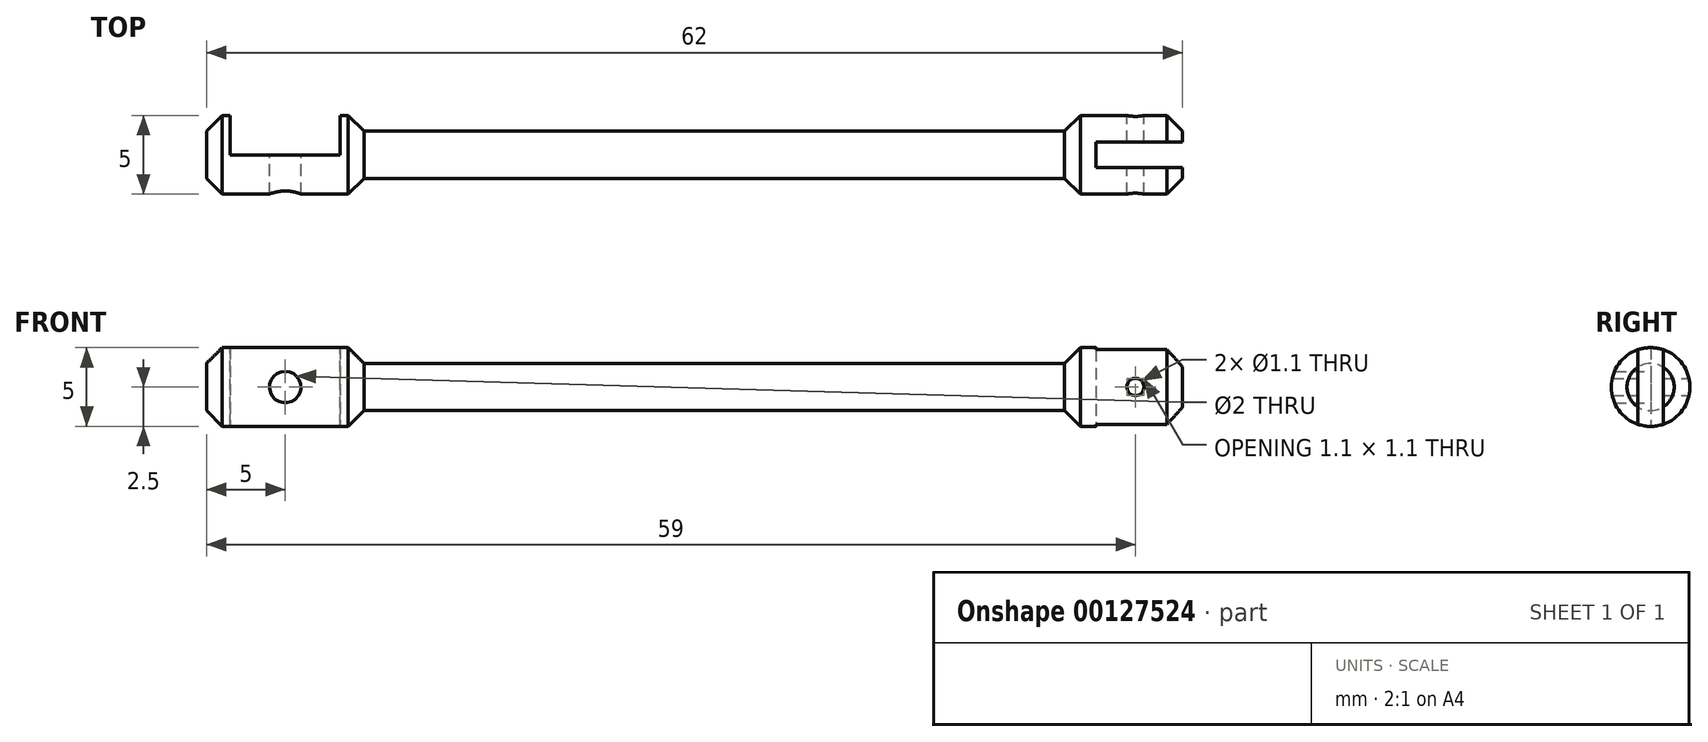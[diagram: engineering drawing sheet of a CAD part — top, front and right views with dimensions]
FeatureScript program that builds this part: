
annotation { "Feature Type Name" : "Feature", "Feature Type Description" : "" }
export const myFeature = defineFeature(function(context is Context, id is Id, definition is map)
    precondition{}
    {
        {
            var Q0;
            Q0=qCreatedBy(makeId("Front.planeOp"),FACE);
            var sketch = newSketch(context, id + "F0", { "sketchPlane" : qUnion([Q0])});
            skCircle(sketch, "E0", {"center": v(0, 0) * mm, "radius": 1 * mm});
            skCircle(sketch, "E1", {"center": v(54, 0) * mm, "radius": 0.55 * mm});
            skLineSegment(sketch, "E2", {"start": v(-5, 0) * mm, "end": v(57, 0) * mm});
            skLineSegment(sketch, "E3", {"start": v(57, 0) * mm, "end": v(57, 1.5) * mm});
            skLineSegment(sketch, "E4", {"start": v(56, 2.5) * mm, "end": v(50.5, 2.5) * mm});
            skLineSegment(sketch, "E5", {"start": v(49.5, 1.5) * mm, "end": v(5, 1.5) * mm});
            skLineSegment(sketch, "E6", {"start": v(4, 2.5) * mm, "end": v(-4, 2.5) * mm});
            skLineSegment(sketch, "E7", {"start": v(-5, 1.5) * mm, "end": v(-5, 0) * mm});
            skLineSegment(sketch, "E8", {"start": v(56, 2.5) * mm, "end": v(57, 1.5) * mm});
            skLineSegment(sketch, "E9", {"start": v(49.5, 1.5) * mm, "end": v(50.5, 2.5) * mm});
            skLineSegment(sketch, "E10", {"start": v(0, 0) * mm, "end": v(0, 0) * mm});
            skLineSegment(sketch, "E11", {"start": v(4, 2.5) * mm, "end": v(5, 1.5) * mm});
            skLineSegment(sketch, "E12", {"start": v(-4, 2.5) * mm, "end": v(-5, 1.5) * mm});
            skSolve(sketch);
        }
        {
            var Q0;
            {var subQ0=sQuery(id+"F0.wireOp",EDGE,"E3");Q0=makeQuery(id+"F0.imprint","IMPRINT",FACE,{"disambiguationData":[TD([[makeQuery(id+"F0.imprint","IMPRINT",EDGE,{"derivedFrom":subQ0}),1.0]])]});}
            var Q1;
            {var subQ0=sQuery(id+"F0.wireOp",EDGE,"E2");var subQ1=sQuery(id+"F0.wireOp",EDGE,"E0");var subQ2=makeQuery(id+"F0.imprint","INTERSECT",VERTEX,{"disambiguationData":[OD(0.0)],"derivedFrom":[subQ1,subQ0]});Q1=makeQuery(id+"F0.imprint","IMPRINT",FACE,{"disambiguationData":[TD([[makeQuery(id+"F0.imprint","IMPRINT",EDGE,{"disambiguationData":[TD([[subQ2,1.0]])],"derivedFrom":subQ1}),1.0]])]});}
            var Q2;
            {var subQ0=sQuery(id+"F0.wireOp",EDGE,"E2");var subQ1=sQuery(id+"F0.wireOp",EDGE,"E1");var subQ2=makeQuery(id+"F0.imprint","INTERSECT",VERTEX,{"disambiguationData":[OD(0.0)],"derivedFrom":[subQ1,subQ0]});Q2=makeQuery(id+"F0.imprint","IMPRINT",FACE,{"disambiguationData":[TD([[makeQuery(id+"F0.imprint","IMPRINT",EDGE,{"disambiguationData":[TD([[subQ2,1.0]])],"derivedFrom":subQ1}),1.0]])]});}
            var Q3;
            Q3=sQuery(id+"F0.wireOp",EDGE,"E2");
            revolve(context, id + "F1", {"entities" : qUnion([Q0, Q1, Q2]), "axis" : qUnion([Q3]), "revolveType" : RevolveType.FULL});
        }
        {
            var Q0;
            {var subQ0=sQuery(id+"F0.wireOp",EDGE,"E2");var subQ1=sQuery(id+"F0.wireOp",EDGE,"E0");var subQ2=makeQuery(id+"F0.imprint","INTERSECT",VERTEX,{"disambiguationData":[OD(0.0)],"derivedFrom":[subQ1,subQ0]});Q0=makeQuery(id+"F0.imprint","IMPRINT",FACE,{"disambiguationData":[TD([[makeQuery(id+"F0.imprint","IMPRINT",EDGE,{"disambiguationData":[TD([[subQ2,-1.0]])],"derivedFrom":subQ1}),1.0]])]});}
            var Q1;
            {var subQ0=sQuery(id+"F0.wireOp",EDGE,"E2");var subQ1=sQuery(id+"F0.wireOp",EDGE,"E0");var subQ2=makeQuery(id+"F0.imprint","INTERSECT",VERTEX,{"disambiguationData":[OD(0.0)],"derivedFrom":[subQ1,subQ0]});Q1=makeQuery(id+"F0.imprint","IMPRINT",FACE,{"disambiguationData":[TD([[makeQuery(id+"F0.imprint","IMPRINT",EDGE,{"disambiguationData":[TD([[subQ2,1.0]])],"derivedFrom":subQ1}),1.0]])]});}
            var Q2;
            {var subQ0=sQuery(id+"F0.wireOp",EDGE,"E2");var subQ1=sQuery(id+"F0.wireOp",EDGE,"E1");var subQ2=makeQuery(id+"F0.imprint","INTERSECT",VERTEX,{"disambiguationData":[OD(0.0)],"derivedFrom":[subQ1,subQ0]});Q2=makeQuery(id+"F0.imprint","IMPRINT",FACE,{"disambiguationData":[TD([[makeQuery(id+"F0.imprint","IMPRINT",EDGE,{"disambiguationData":[TD([[subQ2,-1.0]])],"derivedFrom":subQ1}),1.0]])]});}
            var Q3;
            {var subQ0=sQuery(id+"F0.wireOp",EDGE,"E2");var subQ1=sQuery(id+"F0.wireOp",EDGE,"E1");var subQ2=makeQuery(id+"F0.imprint","INTERSECT",VERTEX,{"disambiguationData":[OD(0.0)],"derivedFrom":[subQ1,subQ0]});Q3=makeQuery(id+"F0.imprint","IMPRINT",FACE,{"disambiguationData":[TD([[makeQuery(id+"F0.imprint","IMPRINT",EDGE,{"disambiguationData":[TD([[subQ2,1.0]])],"derivedFrom":subQ1}),1.0]])]});}
            extrude(context, id + "F2", {"entities" : qUnion([Q0, Q1, Q2, Q3]), "operationType" : NewBodyOperationType.REMOVE, "endBound" : BoundingType.SYMMETRIC, "depth" : 25.4 * mm});
        }
        {
            var Q0;
            Q0=qCreatedBy(makeId("Top.planeOp"),FACE);
            var sketch = newSketch(context, id + "F3", { "sketchPlane" : qUnion([Q0])});
            skLineSegment(sketch, "E13.bottom", {"start": v(-3.5, 4.5) * mm, "end": v(3.5, 4.5) * mm});
            skLineSegment(sketch, "E13.top", {"start": v(-3.5, 0) * mm, "end": v(3.5, 0) * mm});
            skLineSegment(sketch, "E13.left", {"start": v(-3.5, 4.5) * mm, "end": v(-3.5, 0) * mm});
            skLineSegment(sketch, "E13.right", {"start": v(3.5, 4.5) * mm, "end": v(3.5, 0) * mm});
            skLineSegment(sketch, "E14.bottom", {"start": v(57, 0.8) * mm, "end": v(51.5, 0.8) * mm});
            skLineSegment(sketch, "E14.top", {"start": v(57, -0.8) * mm, "end": v(51.5, -0.8) * mm});
            skLineSegment(sketch, "E14.left", {"start": v(57, 0.8) * mm, "end": v(57, -0.8) * mm});
            skLineSegment(sketch, "E14.right", {"start": v(51.5, 0.8) * mm, "end": v(51.5, -0.8) * mm});
            skLineSegment(sketch, "E15", {"start": v(-7.5, 0) * mm, "end": v(53.61, 0) * mm, "construction": true});
            skLineSegment(sketch, "E16", {"start": v(0, 0) * mm, "end": v(0, 7.28) * mm, "construction": true});
            skSolve(sketch);
        }
        {
            var Q0;
            Q0=qSketchRegion(id+"F3",true);
            extrude(context, id + "F4", {"entities" : qUnion([Q0]), "operationType" : NewBodyOperationType.REMOVE, "endBound" : BoundingType.SYMMETRIC, "depth" : 25.4 * mm});
        }
    });
